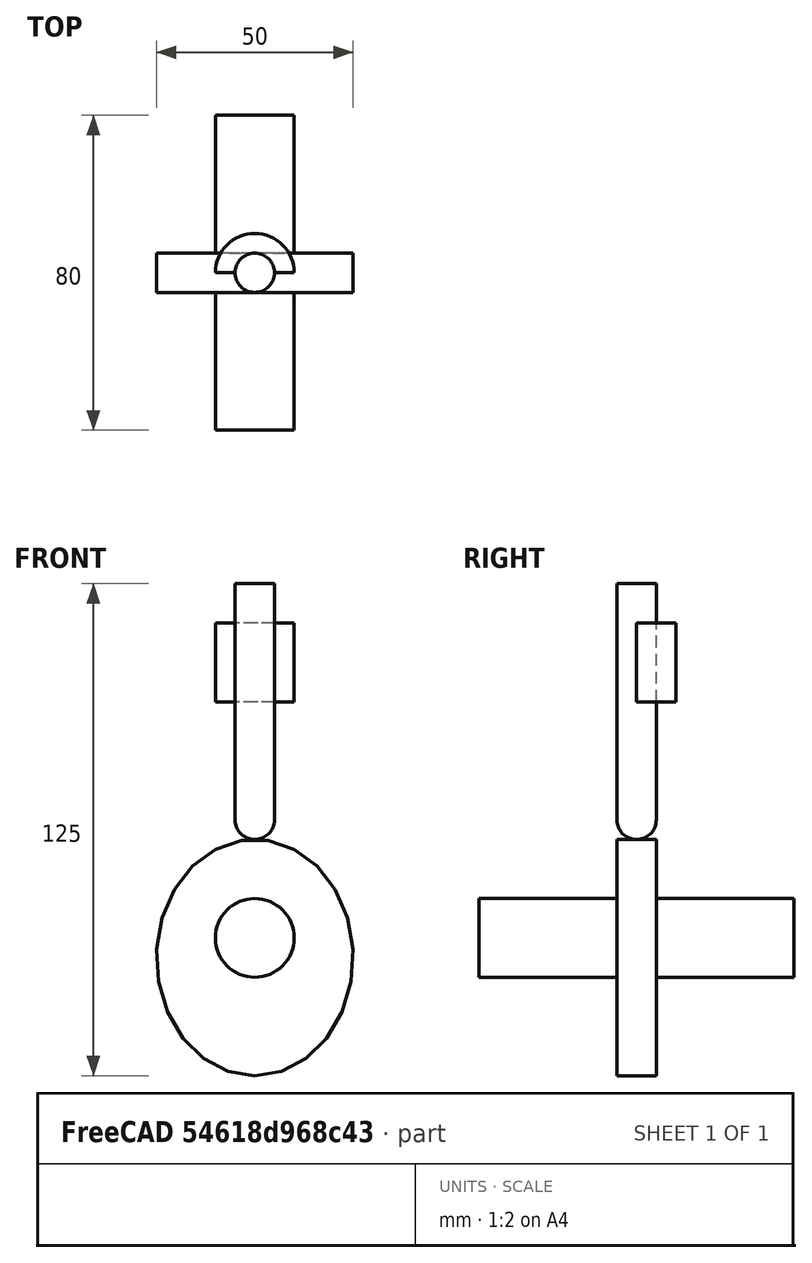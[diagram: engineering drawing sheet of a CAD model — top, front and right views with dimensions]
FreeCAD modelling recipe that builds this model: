
FCSTD DOCUMENT  (FreeCAD 0.18.2R)
Label: CAME
License: All rights reserved
LicenseURL: http://en.wikipedia.org/wiki/All_rights_reserved
objects: Part::Cylinder×4, App::DocumentObjectGroupPython×3, Part::MultiFuse×2, Part::Ellipse×1, Part::Extrusion×1, Part::Sphere×1, Part::Cut×1
note: 10 computed .brp shape members not serialized (recipe doc carries the construction recipe); baked Part::Feature solids carry a one-line shape summary decoded from their .brp

FEATURE [Part::Ellipse] Ellipse
  Angle0 = 0
  Angle1 = 360
  AttacherType = Attacher::AttachEngine3D
  MajorRadius = 30
  MinorRadius = 25
  Placement = pos=(-1.1e-15,-1.1e-15,-5) rot=(-0.57735,-0.57735,0.57735;4.18879rad)
FEATURE [Part::Extrusion] Extrude
  Base = -> Ellipse
  Dir = (0,1,-2e-16)
  DirMode = 2
  FaceMakerClass = Part::FaceMakerBullseye
  LengthFwd = 10
  LengthRev = 0
  Solid = true
  Symmetric = true
FEATURE [Part::Cylinder] Cylinder
  Angle = 360
  AttacherType = Attacher::AttachEngine3D
  Height = 80
  Placement = pos=(0,40,-8.9e-15) rot=(1,0,0;1.5708rad)
  Radius = 10
FEATURE [Part::MultiFuse] Fusion
  Shapes = -> [Extrude,Cylinder]
FEATURE [Part::Sphere] Sphere
  Angle1 = -90
  Angle2 = 90
  Angle3 = 360
  AttacherType = Attacher::AttachEngine3D
  Radius = 5
FEATURE [Part::Cylinder] Cylinder001
  Angle = 360
  AttacherType = Attacher::AttachEngine3D
  Height = 60
  Radius = 5
FEATURE [Part::MultiFuse] Fusion001
  Placement = pos=(0,0,30) rot=(0,0,1;0rad)
  Shapes = -> [Sphere,Cylinder001]
FEATURE [Part::Cylinder] Cylinder002
  Angle = 180
  AttacherType = Attacher::AttachEngine3D
  Height = 20
  Radius = 10
FEATURE [Part::Cylinder] Cylinder003
  Angle = 360
  AttacherType = Attacher::AttachEngine3D
  Height = 20
  Radius = 5
FEATURE [Part::Cut] Cut
  Base = -> Cylinder002
  Placement = pos=(0,0,60) rot=(0,0,1;0rad)
  Tool = -> Cylinder003
FEATURE [App::DocumentObjectGroupPython] My_Placer  # scripted group (container) (typed FeaturePython)
  RotAxis = (0,1,0)
  RotCenter = (0,0,0)
  arc = time*360
  arc0 = 0
  arc1 = 90
  target = -> Fusion
  time = 0
  x = 0
  x0 = 0
  x1 = 200
  y = 0
  y0 = 0
  y1 = 0
  z = 0
  z0 = 0
  z1 = 0
FEATURE [App::DocumentObjectGroupPython] My_Placer001  # scripted group (container) (typed FeaturePython)
  Placement = pos=(0,0,30) rot=(0,0,1;0rad)
  RotAxis = (0,0,1)
  RotCenter = (0,0,0)
  arc = 0
  arc0 = 0
  arc1 = 90
  target = -> Fusion001
  time = 0
  x = 0
  x0 = 1
  x1 = 200
  y = 0
  y0 = 0
  y1 = 0
  z = 35 - 5*x0 - 5*y0**2
  z0 = 0
  z1 = 0
  expr: y0 = sin(time * 360)
  expr: x0 = cos(time * 360)
FEATURE [App::DocumentObjectGroupPython] My_Manager  # scripted group (container) (typed FeaturePython)
  Group = -> [My_Placer,My_Placer001]
  intervall = 1000
  sleeptime = 0.02
  start = 0
  step = 0
  text = NO
